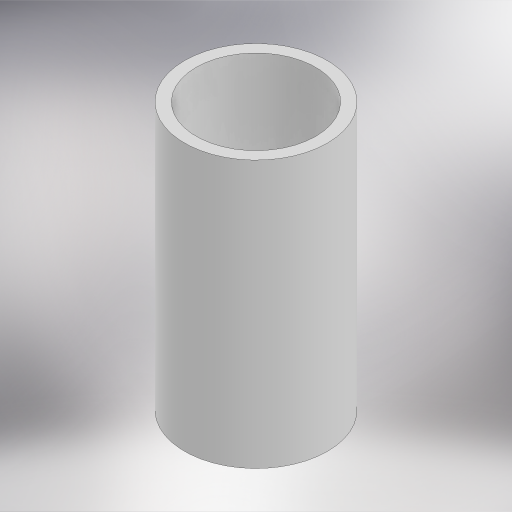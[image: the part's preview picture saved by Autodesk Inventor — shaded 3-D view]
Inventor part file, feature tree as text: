
AUTODESK INVENTOR PART (.ipt)
format: ipt  version: 2023 (Build 270158000, 158)  size: 260,096 bytes
history: native  units: in
note: dims shown in document units (in); Inventor stores cm internally (conversion verified against a paired STEP export)
features: other x1, extrude x1, sketch x1
ambient origin geometry x8: Origin, YZ Plane, XZ Plane, XY Plane, X Axis, Y Axis, Z Axis, Center Point
bodies: Body1 (feature_tree)
feature tree (3):
  other  "Sólido1"
  extrude  "Extrusión1"  Depth=1.5748in
  sketch  "Boceto2"  dims[d0=0.7055in d1=0.8425in d2=1.5748in d3=0.0in]
